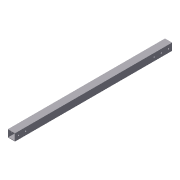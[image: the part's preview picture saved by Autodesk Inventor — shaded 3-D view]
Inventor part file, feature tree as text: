
AUTODESK INVENTOR PART (.ipt)
format: ipt  version: 2012 (Build 160160000, 160)  size: 99,328 bytes
history: native  units: in
note: dims shown in document units (in); Inventor stores cm internally (conversion verified against a paired STEP export)
features: extrude x3, sketch x3, shell x1
ambient origin geometry x8: Origin, YZ Plane, XZ Plane, XY Plane, X Axis, Y Axis, Z Axis, Center Point
bodies: Solid1 (feature_tree)
feature tree (7):
  extrude  "Extrusion1"  Depth=1.0in
  shell  "Shell1"  Thickness=22.0in
  extrude  "Extrusion2"  Depth=0.5in
  extrude  "Extrusion3"  Depth=1.0in
  sketch  "Sketch1"  dims[d0=1.0in d1=1.0in d2=22.0in d3=0.0in]
  sketch  "Sketch2"  dims[d4=0.0625in d5=0.5in]
  sketch  "Sketch3"  dims[d6=0.5in d7=1.0in d8=0.5in d9=0.1875in d10=0.1875in d11=21.0in d12=0.0in d13=0.5in d14=1.0in d15=0.5in d16=0.1875in d17=21.0in d18=0.0in]
